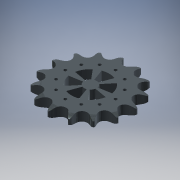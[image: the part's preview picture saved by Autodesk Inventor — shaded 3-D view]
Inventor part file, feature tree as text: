
AUTODESK INVENTOR PART (.ipt)
format: ipt  version: 2016 (Build 200138000, 138)  size: 615,424 bytes
history: native  units: mm
features: other x7, extrude x4, sketch x2, pattern_linear x1, pattern_circular x1
ambient origin geometry x8: Origin, YZ Plane, XZ Plane, XY Plane, X Axis, Y Axis, Z Axis, Center Point
bodies: Solid1 (feature_tree)
feature tree (15):
  other  "outer_drive_sprocket"
  other  "Theoretical Tooth Profile"
  other  "Tooth Profile"
  other  "Section Profile"
  other  "Shroud"
  other  "Strand"
  pattern_linear  "Strand Pattern"  Spacing1=4.29755mm  [1 undecoded]
  extrude  "Theoretical Tooth"  Depth=10.0mm
  extrude  "Tooth"  Depth=10.0mm
  pattern_circular  "Tooth Pattern"  [2 undecoded]
  other  "Timing Plane"
  extrude  "Extrusion4"  Depth=10.0mm
  extrude  "Extrusion5"  Depth=10.0mm
  sketch  "Sketch4"  dims[d0=61.083626mm]
  sketch  "Sketch5"  dims[d2=4.18879mm d3=4.29755mm d10=22.514747mm d11=2.490003mm d12=6.808mm d13=11.10555mm d14=11.914mm d18=10.0mm d19=0.0mm d20=150.0mm d21=360.0deg d23=3.81mm d28=0.0mm d29=0.0mm d30=7.2075mm d31=38.850402mm d32=7.2075mm d33=1.5875mm d34=12.7mm d36=90.0deg d37=90.0deg d38=10.0mm d40=13.92mm d42=0.0mm d43=3.60375mm d44=23.387412mm d45=17.3604mm d46=4.29755mm d47=10.0mm d48=0.0mm d49=0.0mm d50=10.0mm d51=10.0mm d53=30.0mm d87=40.0mm d88=10.0mm d89=30.0mm d92=6.981317mm d93=60.0mm d95=360.0deg d97=10.0mm d98=0.0mm d100=2.35mm d101=120.0mm d103=360.0deg d105=20.0mm d106=0.0mm d107=0.0mm]
note: 3 required parameter values undecoded (feature->parameter linkage not recoverable at this tier; creation-order binding heuristic only, values carry confidence <= 0.55)
